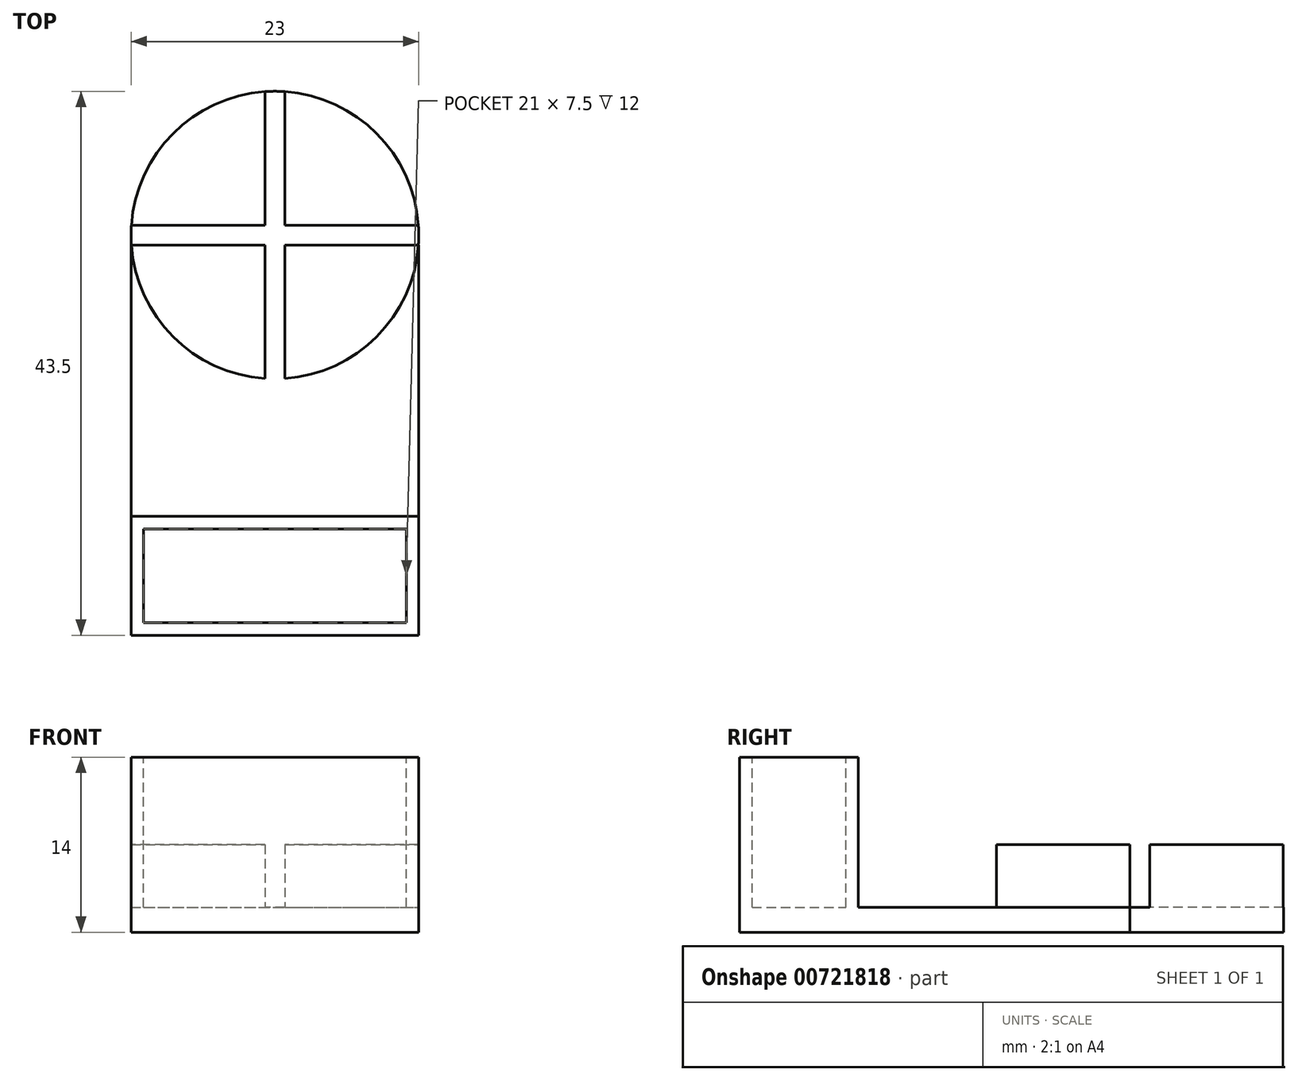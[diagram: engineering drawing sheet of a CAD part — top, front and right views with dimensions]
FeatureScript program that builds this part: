
annotation { "Feature Type Name" : "Feature", "Feature Type Description" : "" }
export const myFeature = defineFeature(function(context is Context, id is Id, definition is map)
    precondition{}
    {
        {
            var Q0;
            Q0=qCreatedBy(makeId("Top.planeOp"),FACE);
            var sketch = newSketch(context, id + "F0", { "sketchPlane" : qUnion([Q0])});
            skArc(sketch, "E0", {"start": v(-0.8, 11.47) * mm, "mid": v(-8.13, 8.13) * mm, "end": v(-11.47, 0.8) * mm});
            skLineSegment(sketch, "E1.top", {"start": v(-11.5, -32) * mm, "end": v(11.5, -32) * mm});
            skLineSegment(sketch, "E1.left", {"start": v(-11.5, -0.8) * mm, "end": v(-11.5, -32) * mm});
            skLineSegment(sketch, "E1.right", {"start": v(11.5, -0.8) * mm, "end": v(11.5, -32) * mm});
            skLineSegment(sketch, "E2.bottom", {"start": v(-11.47, 0.8) * mm, "end": v(-0.8, 0.8) * mm});
            skLineSegment(sketch, "E2.top", {"start": v(-11.5, -0.8) * mm, "end": v(-0.8, -0.8) * mm});
            skLineSegment(sketch, "E3.left", {"start": v(-0.8, 11.47) * mm, "end": v(-0.8, 0.8) * mm});
            skLineSegment(sketch, "E3.right", {"start": v(0.8, 11.47) * mm, "end": v(0.8, 0.8) * mm});
            skPoint(sketch, "E4.orphan", {"position": v(-0.8, 14.26) * mm});
            skPoint(sketch, "E5.orphan", {"position": v(0.8, 14.26) * mm});
            skPoint(sketch, "E6.orphan", {"position": v(-17.98, 0.8) * mm});
            skPoint(sketch, "E7.orphan", {"position": v(-17.98, -0.8) * mm});
            skArc(sketch, "E8.trimOffspring", {"start": v(-11.47, -0.8) * mm, "mid": v(0, -11.5) * mm, "end": v(11.47, -0.8) * mm});
            skArc(sketch, "E9.trimOffspring", {"start": v(11.47, 0.8) * mm, "mid": v(8.13, 8.13) * mm, "end": v(0.8, 11.47) * mm});
            skPoint(sketch, "E10.orphan", {"position": v(17.98, 0.8) * mm});
            skPoint(sketch, "E11.orphan", {"position": v(17.98, -0.8) * mm});
            skLineSegment(sketch, "E12.trimOffspring", {"start": v(0.8, -0.8) * mm, "end": v(0.8, -11.47) * mm});
            skLineSegment(sketch, "E13.trimOffspring", {"start": v(0.8, 0.8) * mm, "end": v(11.47, 0.8) * mm});
            skLineSegment(sketch, "E14.trimOffspring", {"start": v(-0.8, -0.8) * mm, "end": v(-0.8, -11.47) * mm});
            skPoint(sketch, "E1.bottom.start.orphan", {"position": v(-11.5, 0) * mm});
            skLineSegment(sketch, "E15.trimOffspring", {"start": v(0.8, -0.8) * mm, "end": v(11.5, -0.8) * mm});
            skPoint(sketch, "E16.orphan", {"position": v(0.8, -14.26) * mm});
            skPoint(sketch, "E17.orphan", {"position": v(-0.8, -14.26) * mm});
            skCircle(sketch, "E18", {"center": v(0, 0) * mm, "radius": 11.5 * mm});
            skLineSegment(sketch, "E19.bottom", {"start": v(-10.5, -31) * mm, "end": v(10.5, -31) * mm});
            skLineSegment(sketch, "E19.top", {"start": v(-10.5, -23.5) * mm, "end": v(10.5, -23.5) * mm});
            skLineSegment(sketch, "E19.left", {"start": v(-10.5, -31) * mm, "end": v(-10.5, -23.5) * mm});
            skLineSegment(sketch, "E19.right", {"start": v(10.5, -31) * mm, "end": v(10.5, -23.5) * mm});
            skLineSegment(sketch, "E20", {"start": v(-11.5, -22.5) * mm, "end": v(11.5, -22.5) * mm});
            skSolve(sketch);
        }
        {
            var Q0;
            {var subQ2=sQuery(id+"F0.wireOp",EDGE,"E12.trimOffspring");var subQ3=makeQuery(id+"F0.imprint","IMPRINT",EDGE,{"derivedFrom":subQ2});var subQ6=sQuery(id+"F0.wireOp",EDGE,"E14.trimOffspring");var subQ9=makeQuery(id+"F0.imprint","IMPRINT",EDGE,{"derivedFrom":subQ6});var subQ10=sQuery(id+"F0.wireOp",EDGE,"E2.bottom");var subQ11=makeQuery(id+"F0.imprint","IMPRINT",EDGE,{"derivedFrom":subQ10});var subQ20=sQuery(id+"F0.wireOp",EDGE,"E0");var subQ22=sQuery(id+"F0.wireOp",EDGE,"E3.right");var subQ24=makeQuery(id+"F0.imprint","IMPRINT",EDGE,{"derivedFrom":subQ22});var subQ30=sQuery(id+"F0.wireOp",EDGE,"E20");var subQ34=makeQuery(id+"F0.imprint","IMPRINT",EDGE,{"derivedFrom":subQ30});var subQ35=sQuery(id+"F0.wireOp",EDGE,"E1.top");Q0=qUnion([makeQuery(id+"F0.imprint","IMPRINT",FACE,{"disambiguationData":[TD([[makeQuery(id+"F0.imprint","IMPRINT",EDGE,{"derivedFrom":subQ20}),1.0]])]}),makeQuery(id+"F0.imprint","IMPRINT",FACE,{"disambiguationData":[TD([[subQ24,1.0]])]}),makeQuery(id+"F0.imprint","IMPRINT",FACE,{"disambiguationData":[TD([[makeQuery(id+"F0.imprint","IMPRINT",EDGE,{"derivedFrom":subQ35}),1.0]])]}),makeQuery(id+"F0.imprint","IMPRINT",FACE,{"disambiguationData":[TD([[subQ9,-1.0]])]}),makeQuery(id+"F0.imprint","IMPRINT",FACE,{"disambiguationData":[TD([[subQ3,1.0]])]}),makeQuery(id+"F0.imprint","IMPRINT",FACE,{"disambiguationData":[TD([[subQ34,1.0]])]}),makeQuery(id+"F0.imprint","IMPRINT",FACE,{"disambiguationData":[TD([[subQ11,-1.0]])]})]);}
            extrude(context, id + "F1", {"entities" : qUnion([Q0]), "oppositeDirection" : true, "depth" : 2 * mm, "offsetDistance" : 25 * mm});
        }
        {
            var Q0;
            Q0=makeQuery(id+"F0.imprint","IMPRINT",FACE,{"disambiguationData":[TD([[makeQuery(id+"F0.imprint","IMPRINT",EDGE,{"derivedFrom":sQuery(id+"F0.wireOp",EDGE,"E0")}),1.0]])]});
            var Q1;
            Q1=makeQuery(id+"F0.imprint","IMPRINT",FACE,{"disambiguationData":[TD([[makeQuery(id+"F0.imprint","IMPRINT",EDGE,{"derivedFrom":sQuery(id+"F0.wireOp",EDGE,"E3.right")}),1.0]])]});
            var Q2;
            {var subQ3=sQuery(id+"F0.wireOp",EDGE,"E12.trimOffspring");Q2=makeQuery(id+"F0.imprint","IMPRINT",FACE,{"disambiguationData":[TD([[makeQuery(id+"F0.imprint","IMPRINT",EDGE,{"derivedFrom":subQ3}),1.0]])]});}
            var Q3;
            {var subQ3=sQuery(id+"F0.wireOp",EDGE,"E14.trimOffspring");Q3=makeQuery(id+"F0.imprint","IMPRINT",FACE,{"disambiguationData":[TD([[makeQuery(id+"F0.imprint","IMPRINT",EDGE,{"derivedFrom":subQ3}),-1.0]])]});}
            var Q4;
            {var subQ1=sQuery(id+"F0.wireOp",EDGE,"E1.top");Q4=makeQuery(id+"F0.imprint","IMPRINT",FACE,{"disambiguationData":[TD([[makeQuery(id+"F0.imprint","IMPRINT",EDGE,{"derivedFrom":subQ1}),1.0]])]});}
            extrude(context, id + "F2", {"entities" : qUnion([Q0, Q1, Q2, Q3, Q4]), "operationType" : NewBodyOperationType.ADD, "depth" : 5 * mm, "offsetDistance" : 25 * mm});
        }
        {
            var Q0;
            Q0=makeQuery(id+"F2.opExtrude","CAP_FACE",FACE,{"disambiguationData":[OSD([sQuery(id+"F0.wireOp",EDGE,"E1.top"),sQuery(id+"F0.wireOp",EDGE,"E1.left"),sQuery(id+"F0.wireOp",EDGE,"E1.right"),sQuery(id+"F0.wireOp",EDGE,"E19.bottom"),sQuery(id+"F0.wireOp",EDGE,"E19.top"),sQuery(id+"F0.wireOp",EDGE,"E19.left"),sQuery(id+"F0.wireOp",EDGE,"E19.right"),sQuery(id+"F0.wireOp",EDGE,"E20")])],"isStart":false});
            extrude(context, id + "F3", {"entities" : qUnion([Q0]), "operationType" : NewBodyOperationType.ADD, "depth" : 7 * mm, "offsetDistance" : 25 * mm});
        }
        {
            var Q0;
            Q0=makeQuery(id+"F0.imprint","IMPRINT",FACE,{"disambiguationData":[TD([[makeQuery(id+"F0.imprint","IMPRINT",EDGE,{"derivedFrom":sQuery(id+"F0.wireOp",EDGE,"E19.bottom")}),1.0]])]});
            extrude(context, id + "F4", {"entities" : qUnion([Q0]), "operationType" : NewBodyOperationType.ADD, "oppositeDirection" : true, "depth" : 2 * mm, "offsetDistance" : 25 * mm});
        }
    });
